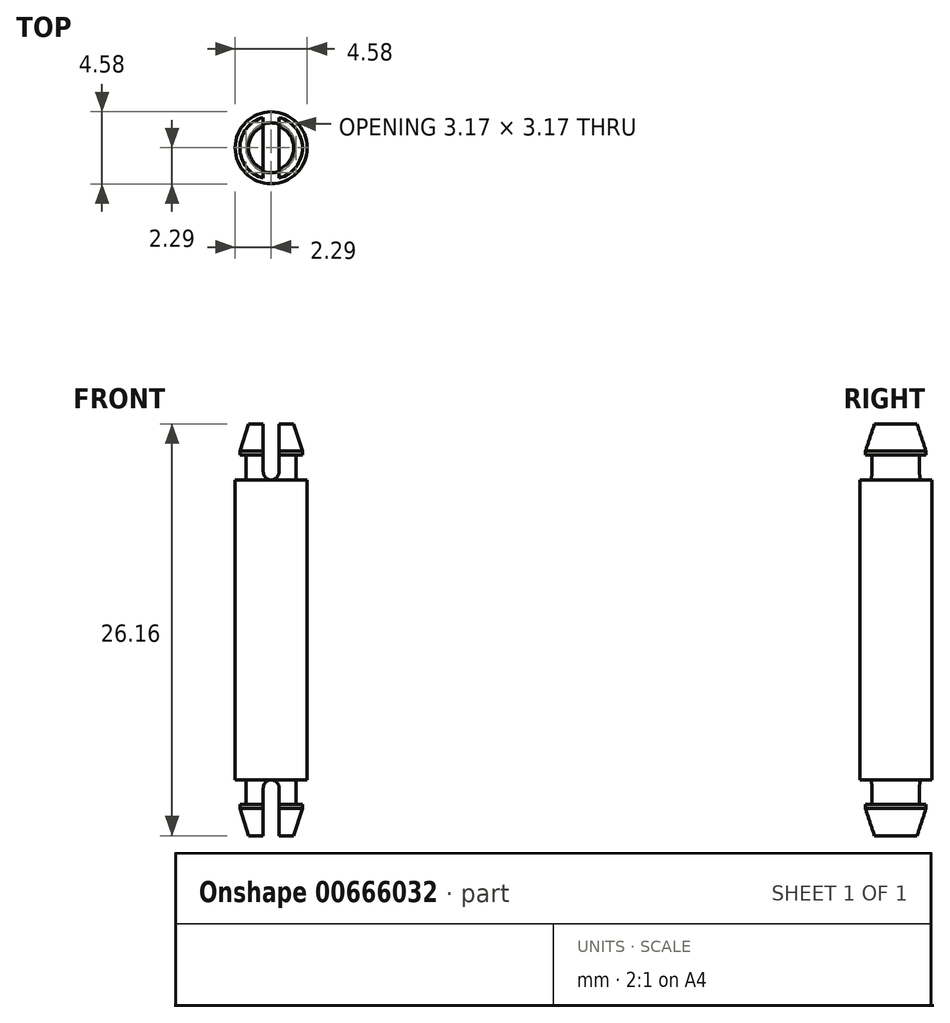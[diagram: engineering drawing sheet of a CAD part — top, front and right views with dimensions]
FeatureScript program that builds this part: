
annotation { "Feature Type Name" : "Feature", "Feature Type Description" : "" }
export const myFeature = defineFeature(function(context is Context, id is Id, definition is map)
    precondition{}
    {
        {
            var Q0;
            Q0=qCreatedBy(makeId("Top.planeOp"),FACE);
            var sketch = newSketch(context, id + "F0", { "sketchPlane" : qUnion([Q0])});
            skCircle(sketch, "E0", {"center": v(0, 0) * mm, "radius": 2.29 * mm});
            skSolve(sketch);
        }
        {
            var Q0;
            Q0 = qSketchRegion(id + "F0", true);
            extrude(context, id + "F1", {"entities" : qUnion([Q0]), "depth" : 19.05 * mm / 2, "offsetDistance" : 25 * mm});
        }
        {
            var Q0;
            Q0=makeQuery(id+"F1.opExtrude","CAP_FACE",FACE,{"disambiguationData":[OSD([sQuery(id+"F0.wireOp",EDGE,"E0")])],"isStart":false});
            cPlane(context, id + "F2", {"entities" : qUnion([Q0]), "cplaneType" : CPlaneType.OFFSET, "offset" : 0 * mm, "width" : 150 * mm, "height" : 150 * mm});
        }
        {
            var Q0;
            Q0=qCreatedBy(id+"F2.planeOp",FACE);
            var sketch = newSketch(context, id + "F3", { "sketchPlane" : qUnion([Q0])});
            skCircle(sketch, "E1", {"center": v(0, 0) * mm, "radius": 1.59 * mm});
            skSolve(sketch);
        }
        {
            var Q0;
            Q0 = qSketchRegion(id + "F3", true);
            extrude(context, id + "F4", {"entities" : qUnion([Q0]), "operationType" : NewBodyOperationType.ADD, "depth" : 1.57 * mm, "offsetDistance" : 25 * mm});
        }
        {
            var Q0;
            Q0=makeQuery(id+"F4.opExtrude","CAP_FACE",FACE,{"disambiguationData":[OSD([sQuery(id+"F3.wireOp",EDGE,"E1")])],"isStart":false});
            cPlane(context, id + "F5", {"entities" : qUnion([Q0]), "cplaneType" : CPlaneType.OFFSET, "offset" : 0 * mm, "width" : 150 * mm, "height" : 150 * mm});
        }
        {
            var Q0;
            Q0=qCreatedBy(id+"F5.planeOp",FACE);
            var sketch = newSketch(context, id + "F6", { "sketchPlane" : qUnion([Q0])});
            skCircle(sketch, "E2", {"center": v(0, 0) * mm, "radius": 1.99 * mm});
            skSolve(sketch);
        }
        {
            var Q0;
            Q0=qCreatedBy(id+"F2.planeOp",FACE);
            cPlane(context, id + "F7", {"entities" : qUnion([Q0]), "cplaneType" : CPlaneType.OFFSET, "offset" : 3.56 * mm, "width" : 150 * mm, "height" : 150 * mm});
        }
        {
            var Q0;
            Q0=makeQuery(id+"F6.imprint","IMPRINT",FACE,{"disambiguationData":[TD([[makeQuery(id+"F6.imprint","IMPRINT",EDGE,{"derivedFrom":sQuery(id+"F6.wireOp",EDGE,"E2")}),1.0]])]});
            var Q1;
            Q1=sQuery(id+"F6.wireOp",EDGE,"E2");
            extrude(context, id + "F8", {"entities" : qUnion([Q0]), "operationType" : NewBodyOperationType.ADD, "surfaceEntities" : qUnion([Q1]), "depth" : .25 * mm, "offsetDistance" : 25 * mm});
        }
        {
            var Q0;
            Q0=qCreatedBy(id+"F7.planeOp",FACE);
            var sketch = newSketch(context, id + "F9", { "sketchPlane" : qUnion([Q0])});
            skCircle(sketch, "E3.0", {"center": v(0, 0) * mm, "radius": 1.59 * mm, "construction": true});
            skCircle(sketch, "E4", {"center": v(0, 0) * mm, "radius": 1.44 * mm});
            skSolve(sketch);
        }
        {
            var Q1;
            Q1=makeQuery(id+"F9.imprint","IMPRINT",FACE,{"disambiguationData":[TD([[makeQuery(id+"F9.imprint","IMPRINT",EDGE,{"derivedFrom":sQuery(id+"F9.wireOp",EDGE,"E4")}),1.0]])]});
            var Q2;
            Q2=makeQuery(id+"F8.opExtrude","CAP_FACE",FACE,{"disambiguationData":[OSD([sQuery(id+"F6.wireOp",EDGE,"E2")])],"isStart":false});
            loft(context, id + "F10", {"operationType" : NewBodyOperationType.ADD, "sheetProfilesArray" : [{ "sheetProfileEntities" : qUnion([Q1]) }, { "sheetProfileEntities" : qUnion([Q2]) }]});
        }
        {
            var Q0;
            Q0=qCreatedBy(makeId("Front.planeOp"),FACE);
            var sketch = newSketch(context, id + "F11", { "sketchPlane" : qUnion([Q0])});
            skLineSegment(sketch, "E5", {"start": v(0, -1.01) * mm, "end": v(0, 14.36) * mm, "construction": true});
            skLineSegment(sketch, "E6.bottom", {"start": v(-0.5, 13.08) * mm, "end": v(0.5, 13.08) * mm});
            skLineSegment(sketch, "E6.top", {"start": v(0, 9.53) * mm, "end": v(0, 9.53) * mm});
            skLineSegment(sketch, "E6.left", {"start": v(-0.5, 13.08) * mm, "end": v(-0.5, 10.03) * mm});
            skLineSegment(sketch, "E6.right", {"start": v(0.5, 13.08) * mm, "end": v(0.5, 10.03) * mm});
            skPoint(sketch, "E7", {"position": v(0, 9.53) * mm});
            skPoint(sketch, "E8.visualSharp", {"position": v(-0.5, 9.53) * mm});
            skArc(sketch, "E8.filletArc", {"start": v(-0.5, 10.03) * mm, "mid": v(-0.35, 9.67) * mm, "end": v(0, 9.53) * mm});
            skPoint(sketch, "E9.visualSharp", {"position": v(0.5, 9.53) * mm});
            skArc(sketch, "E9.filletArc", {"start": v(0, 9.53) * mm, "mid": v(0.35, 9.67) * mm, "end": v(0.5, 10.03) * mm});
            skSolve(sketch);
        }
        {
            var Q0;
            Q0 = qSketchRegion(id + "F11", true);
            extrude(context, id + "F12", {"entities" : qUnion([Q0]), "operationType" : NewBodyOperationType.REMOVE, "endBound" : BoundingType.THROUGH_ALL, "oppositeDirection" : true, "depth" : 25 * mm, "offsetDistance" : 25 * mm, "hasSecondDirection" : true, "secondDirectionBound" : SecondDirectionBoundingType.THROUGH_ALL, "secondDirectionOppositeDirection" : false, "secondDirectionDepth" : 25 * mm});
        }
        {
            var Q0;
            Q0=makeQuery(id+"F1.opExtrude","SWEPT_BODY",BODY,{"disambiguationData":[OSD([sQuery(id+"F0.wireOp",EDGE,"E0")])]});
            var Q1;
            Q1=qCreatedBy(makeId("Top.planeOp"),FACE);
            mirror(context, id + "F13", {"operationType" : NewBodyOperationType.ADD, "entities" : qUnion([Q0]), "mirrorPlane" : qUnion([Q1])});
        }
    });
